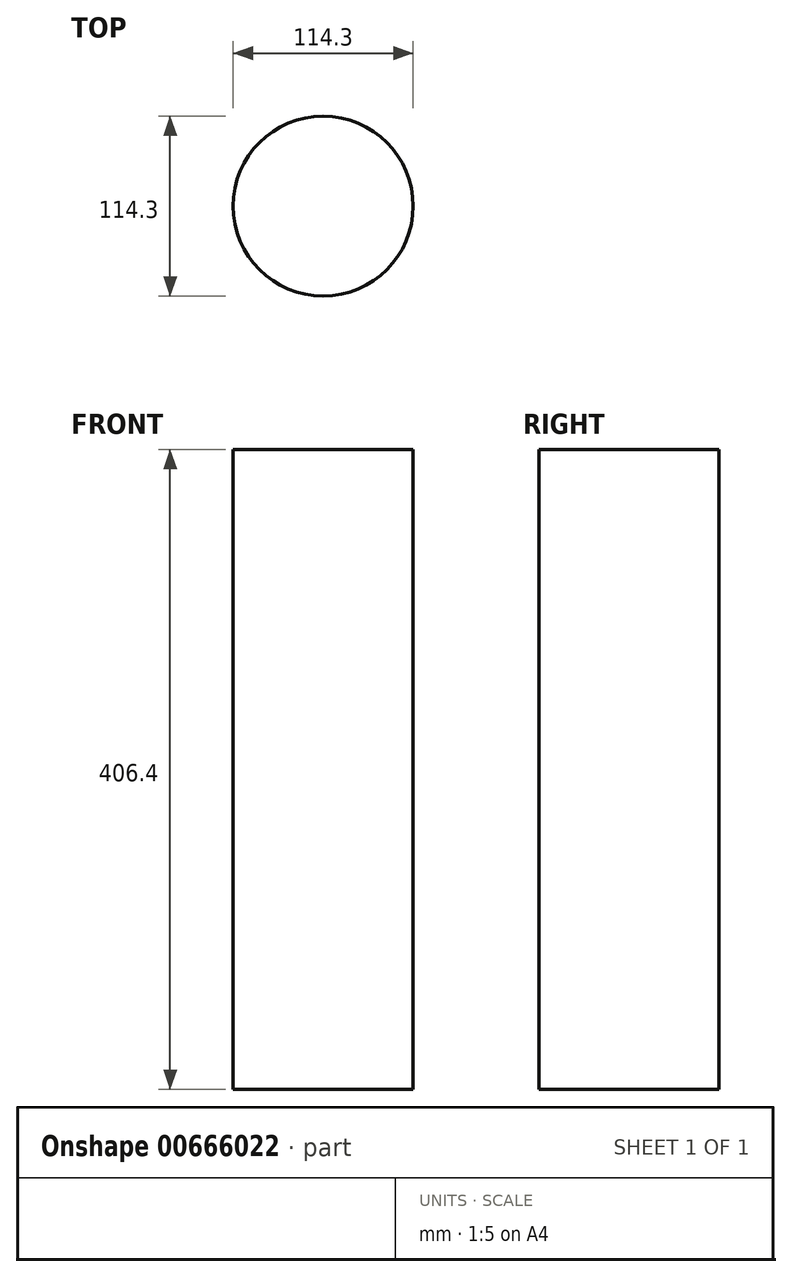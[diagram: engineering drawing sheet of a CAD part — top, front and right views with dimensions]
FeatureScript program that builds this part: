
annotation { "Feature Type Name" : "Feature", "Feature Type Description" : "" }
export const myFeature = defineFeature(function(context is Context, id is Id, definition is map)
    precondition{}
    {
        {
            var Q0;
            Q0=qCreatedBy(makeId("Top.planeOp"),FACE);
            var sketch = newSketch(context, id + "F0", { "sketchPlane" : qUnion([Q0])});
            skCircle(sketch, "E0", {"center": v(-74.12, 12.88) * mm, "radius": 57.15 * mm});
            skSolve(sketch);
        }
        {
            var Q0;
            Q0 = qSketchRegion(id + "F0", true);
            extrude(context, id + "F1", {"entities" : qUnion([Q0]), "depth" : 406.4 * mm, "offsetDistance" : 25.4 * mm});
        }
    });
